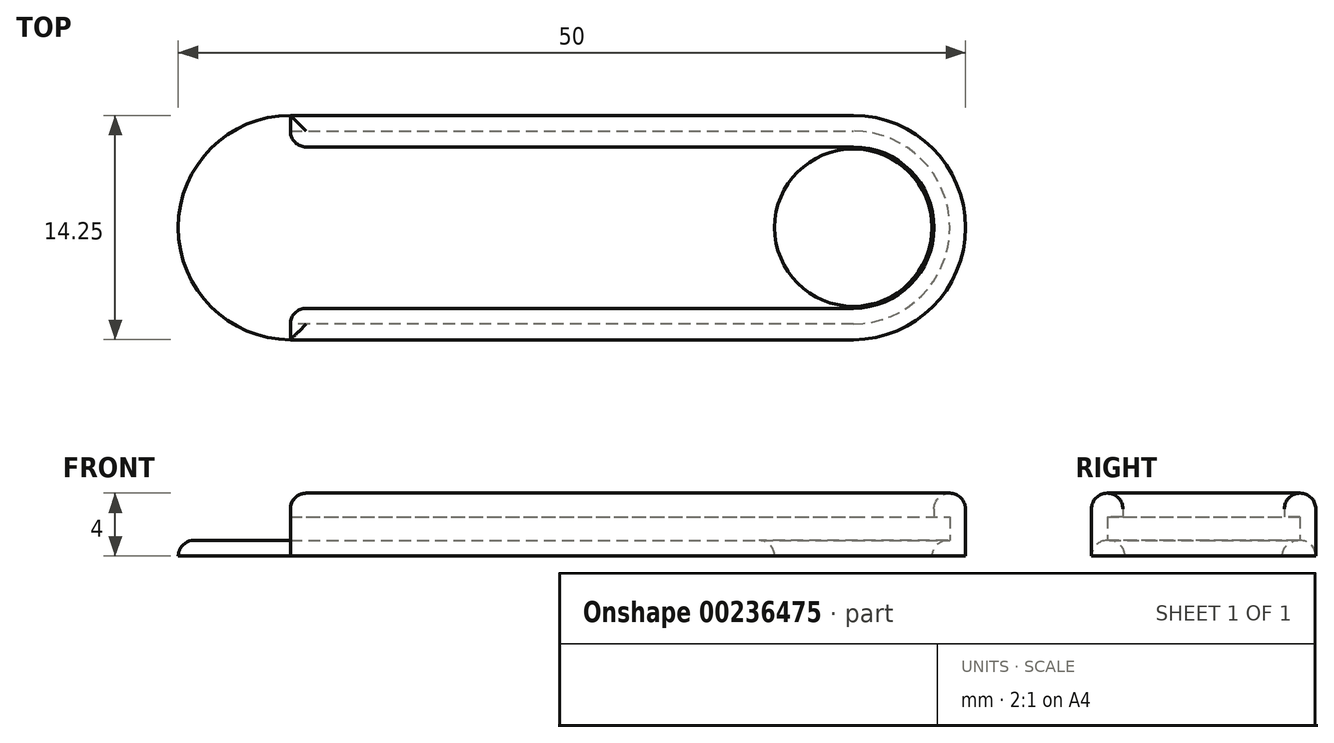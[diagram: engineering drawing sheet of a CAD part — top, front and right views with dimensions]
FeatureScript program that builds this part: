
annotation { "Feature Type Name" : "Feature", "Feature Type Description" : "" }
export const myFeature = defineFeature(function(context is Context, id is Id, definition is map)
    precondition{}
    {
        {
            var Q0;
            Q0=qCreatedBy(makeId("Top.planeOp"),FACE);
            var sketch = newSketch(context, id + "F0", { "sketchPlane" : qUnion([Q0])});
            skArc(sketch, "E0", {"start": v(23.3, -6.12) * mm, "mid": v(29.42, 0) * mm, "end": v(23.3, 6.13) * mm});
            skArc(sketch, "E1", {"start": v(-12.46, 6.12) * mm, "mid": v(-18.58, 0) * mm, "end": v(-12.46, -6.12) * mm});
            skPoint(sketch, "E2", {"position": v(-12.46, 6.12) * mm});
            skPoint(sketch, "E3", {"position": v(-12.46, -6.12) * mm});
            skPoint(sketch, "E4", {"position": v(23.3, 6.13) * mm});
            skPoint(sketch, "E5", {"position": v(23.3, -6.12) * mm});
            skLineSegment(sketch, "E6", {"start": v(-12.46, 6.13) * mm, "end": v(23.3, 6.13) * mm});
            skLineSegment(sketch, "E7", {"start": v(23.3, -6.12) * mm, "end": v(-12.46, -6.12) * mm});
            skCircle(sketch, "E8", {"center": v(23.3, 0) * mm, "radius": 5 * mm});
            skLineSegment(sketch, "E9.0", {"start": v(-12.46, 7.13) * mm, "end": v(23.3, 7.13) * mm});
            skArc(sketch, "E9.1", {"start": v(-12.46, 7.12) * mm, "mid": v(-19.58, 0) * mm, "end": v(-12.46, -7.12) * mm});
            skLineSegment(sketch, "E9.2", {"start": v(23.3, -7.12) * mm, "end": v(-12.46, -7.12) * mm});
            skArc(sketch, "E9.3", {"start": v(23.3, -7.12) * mm, "mid": v(30.42, 0) * mm, "end": v(23.3, 7.13) * mm});
            skLineSegment(sketch, "E10", {"start": v(-12.46, 7.13) * mm, "end": v(-12.46, 6.12) * mm});
            skLineSegment(sketch, "E11", {"start": v(-12.46, -6.12) * mm, "end": v(-12.46, -7.12) * mm});
            skSolve(sketch);
        }
        {
            var Q0;
            Q0=makeQuery(id+"F0.imprint","IMPRINT",FACE,{"disambiguationData":[TD([[makeQuery(id+"F0.imprint","IMPRINT",EDGE,{"derivedFrom":sQuery(id+"F0.wireOp",EDGE,"E0")}),1.0]])]});
            var Q1;
            Q1=makeQuery(id+"F0.imprint","IMPRINT",FACE,{"disambiguationData":[TD([[makeQuery(id+"F0.imprint","IMPRINT",EDGE,{"derivedFrom":sQuery(id+"F0.wireOp",EDGE,"E1")}),-1.0]])]});
            extrude(context, id + "F1", {"entities" : qUnion([Q0, Q1]), "depth" : 1 * mm, "offsetDistance" : 25 * mm});
        }
        {
            var Q0;
            Q0=makeQuery(id+"F0.imprint","IMPRINT",FACE,{"disambiguationData":[TD([[makeQuery(id+"F0.imprint","IMPRINT",EDGE,{"derivedFrom":sQuery(id+"F0.wireOp",EDGE,"E0")}),-1.0]])]});
            extrude(context, id + "F2", {"entities" : qUnion([Q0]), "operationType" : NewBodyOperationType.ADD, "depth" : 2.5 * mm, "offsetDistance" : 25 * mm});
        }
        {
            var Q0;
            Q0=makeQuery(id+"F2.opExtrude","CAP_FACE",FACE,{"disambiguationData":[OSD([sQuery(id+"F0.wireOp",EDGE,"E0"),sQuery(id+"F0.wireOp",EDGE,"E6"),sQuery(id+"F0.wireOp",EDGE,"E7"),sQuery(id+"F0.wireOp",EDGE,"E9.0"),sQuery(id+"F0.wireOp",EDGE,"E9.2"),sQuery(id+"F0.wireOp",EDGE,"E9.3"),sQuery(id+"F0.wireOp",EDGE,"E10"),sQuery(id+"F0.wireOp",EDGE,"E11")])],"isStart":false});
            var sketch = newSketch(context, id + "F3", { "sketchPlane" : qUnion([Q0])});
            skArc(sketch, "E12", {"start": v(23.3, -7.12) * mm, "mid": v(30.42, 0) * mm, "end": v(23.3, 7.13) * mm});
            skPoint(sketch, "E13", {"position": v(-12.46, 7.13) * mm});
            skPoint(sketch, "E14", {"position": v(-12.46, -7.12) * mm});
            skPoint(sketch, "E15", {"position": v(-12.46, 0) * mm});
            skArc(sketch, "E16", {"start": v(-12.46, 7.13) * mm, "mid": v(-19.58, 0) * mm, "end": v(-12.46, -7.12) * mm});
            skLineSegment(sketch, "E17", {"start": v(-12.46, 7.13) * mm, "end": v(23.3, 7.13) * mm});
            skLineSegment(sketch, "E18", {"start": v(23.3, -7.12) * mm, "end": v(-12.46, -7.12) * mm});
            skPoint(sketch, "E19", {"position": v(23.3, 7.13) * mm});
            skPoint(sketch, "E20", {"position": v(23.3, -7.12) * mm});
            skArc(sketch, "E21.0", {"start": v(23.3, -5.12) * mm, "mid": v(28.42, 0) * mm, "end": v(23.3, 5.13) * mm});
            skLineSegment(sketch, "E21.1", {"start": v(23.3, -5.12) * mm, "end": v(-12.46, -5.12) * mm});
            skArc(sketch, "E21.2", {"start": v(-12.46, 5.13) * mm, "mid": v(-17.58, 0) * mm, "end": v(-12.46, -5.12) * mm});
            skLineSegment(sketch, "E21.3", {"start": v(-12.46, 5.12) * mm, "end": v(23.3, 5.13) * mm});
            skLineSegment(sketch, "E22", {"start": v(-12.46, 7.13) * mm, "end": v(-12.46, 5.13) * mm});
            skLineSegment(sketch, "E23", {"start": v(-12.46, -5.12) * mm, "end": v(-12.46, -7.12) * mm});
            skSolve(sketch);
        }
        {
            var Q0;
            Q0=makeQuery(id+"F3.imprint","IMPRINT",FACE,{"disambiguationData":[TD([[makeQuery(id+"F3.imprint","IMPRINT",EDGE,{"derivedFrom":sQuery(id+"F3.wireOp",EDGE,"E12")}),1.0]])]});
            var Q1;
            Q1=makeQuery(id+"F3.imprint","IMPRINT",FACE,{"disambiguationData":[TD([[makeQuery(id+"F3.imprint","IMPRINT",EDGE,{"derivedFrom":sQuery(id+"F3.wireOp",EDGE,"E21.0")}),-1.0]])]});
            extrude(context, id + "F4", {"entities" : qUnion([Q0, Q1]), "operationType" : NewBodyOperationType.ADD, "depth" : 1.5 * mm, "offsetDistance" : 25 * mm});
        }
        {
            var Q0;
            Q0=makeQuery(id+"F4.opExtrude","CAP_FACE",FACE,{"disambiguationData":[OSD([sQuery(id+"F3.wireOp",EDGE,"E12"),sQuery(id+"F3.wireOp",EDGE,"E16"),sQuery(id+"F3.wireOp",EDGE,"E17"),sQuery(id+"F3.wireOp",EDGE,"E18"),sQuery(id+"F3.wireOp",EDGE,"E21.0"),sQuery(id+"F3.wireOp",EDGE,"E21.1"),sQuery(id+"F3.wireOp",EDGE,"E21.2"),sQuery(id+"F3.wireOp",EDGE,"E21.3")])],"isStart":false});
            var Q1;
            Q1=makeQuery(id+"F1.opExtrude","CAP_EDGE",EDGE,{"disambiguationData":[OSD([sQuery(id+"F0.wireOp",EDGE,"E8")])],"isStart":false});
            var Q2;
            Q2=makeQuery(id+"F4.opExtrude","SWEPT_EDGE",EDGE,{"disambiguationData":[OSD([sQuery(id+"F3.wireOp",EDGE,"E21.1"),sQuery(id+"F3.wireOp",EDGE,"E21.2"),sQuery(id+"F3.wireOp",EDGE,"E23")])]});
            var Q3;
            Q3=makeQuery(id+"F4.opExtrude","SWEPT_EDGE",EDGE,{"disambiguationData":[OSD([sQuery(id+"F3.wireOp",EDGE,"E21.2"),sQuery(id+"F3.wireOp",EDGE,"E21.3"),sQuery(id+"F3.wireOp",EDGE,"E22")])]});
            var Q4;
            Q4=makeQuery(id+"F1.opExtrude","CAP_EDGE",EDGE,{"disambiguationData":[OSD([sQuery(id+"F0.wireOp",EDGE,"E9.1")])],"isStart":false});
            fillet(context, id + "F5", {"entities" : qUnion([Q0, Q1, Q2, Q3, Q4]), "tangentPropagation" : true, "radius" : 1 * mm, "defaultsChanged" : false, "vertexSettings" : [], "allowEdgeOverflow" : false});
        }
    });
